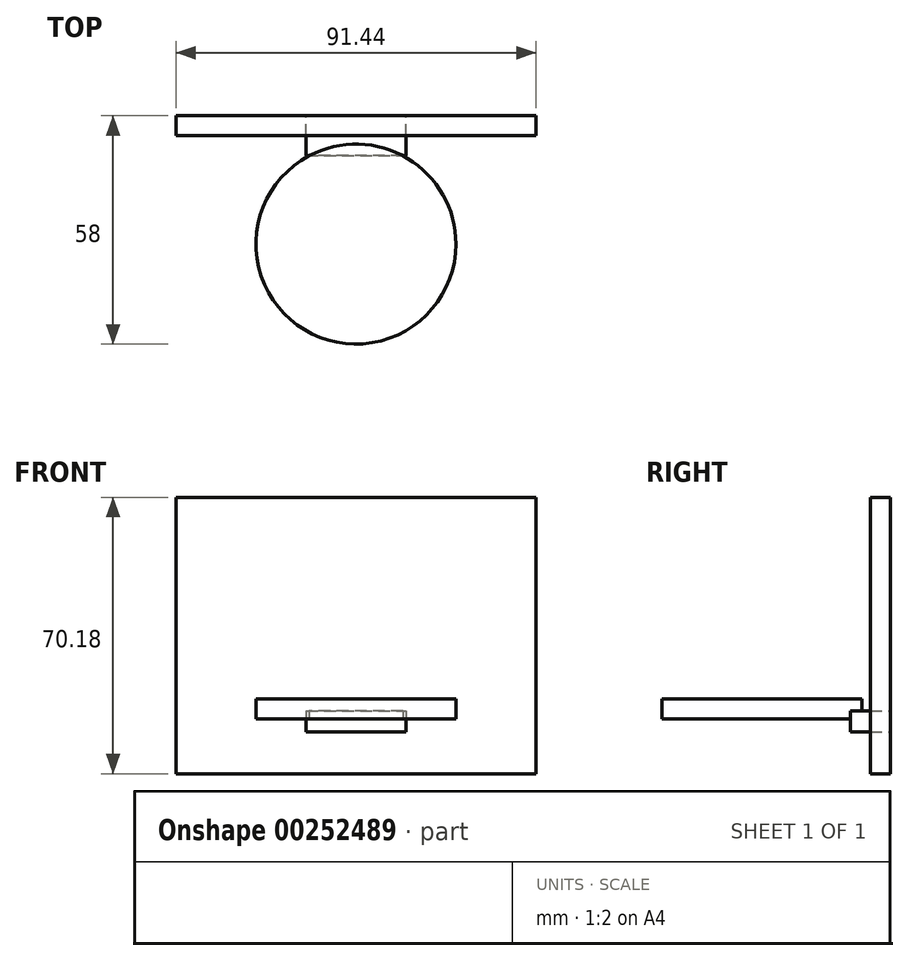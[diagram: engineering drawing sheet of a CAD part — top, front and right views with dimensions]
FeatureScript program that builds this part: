
annotation { "Feature Type Name" : "Feature", "Feature Type Description" : "" }
export const myFeature = defineFeature(function(context is Context, id is Id, definition is map)
    precondition{}
    {
        {
            var Q0;
            Q0=qCreatedBy(makeId("Front.planeOp"),FACE);
            var sketch = newSketch(context, id + "F0", { "sketchPlane" : qUnion([Q0])});
            skLineSegment(sketch, "E0.bottom", {"start": v(-45.72, 56.26) * mm, "end": v(45.72, 56.26) * mm});
            skLineSegment(sketch, "E0.top", {"start": v(-45.72, -13.92) * mm, "end": v(45.72, -13.92) * mm});
            skLineSegment(sketch, "E0.left", {"start": v(-45.72, 56.26) * mm, "end": v(-45.72, -13.92) * mm});
            skLineSegment(sketch, "E0.right", {"start": v(45.72, 56.26) * mm, "end": v(45.72, -13.92) * mm});
            skSolve(sketch);
        }
        {
            var Q0;
            Q0 = qSketchRegion(id + "F0", true);
            extrude(context, id + "F1", {"entities" : qUnion([Q0]), "depth" : 5.08 * mm});
        }
        {
            var Q0;
            Q0=qCreatedBy(makeId("Front.planeOp"),FACE);
            var sketch = newSketch(context, id + "F2", { "sketchPlane" : qUnion([Q0])});
            skLineSegment(sketch, "E1.bottom", {"start": v(-12.7, 2.04) * mm, "end": v(12.7, 2.04) * mm});
            skLineSegment(sketch, "E1.top", {"start": v(-12.7, -3.28) * mm, "end": v(12.7, -3.28) * mm});
            skLineSegment(sketch, "E1.left", {"start": v(-12.7, 2.04) * mm, "end": v(-12.7, -3.28) * mm});
            skLineSegment(sketch, "E1.right", {"start": v(12.7, 2.04) * mm, "end": v(12.7, -3.28) * mm});
            skSolve(sketch);
        }
        {
            var Q0;
            Q0 = qSketchRegion(id + "F2", true);
            extrude(context, id + "F3", {"entities" : qUnion([Q0]), "depth" : 10.16 * mm});
        }
        {
            var Q0;
            Q0=qCreatedBy(makeId("Top.planeOp"),FACE);
            var sketch = newSketch(context, id + "F4", { "sketchPlane" : qUnion([Q0])});
            skCircle(sketch, "E2", {"center": v(0, -32.6) * mm, "radius": 25.4 * mm});
            skSolve(sketch);
        }
        {
            var Q0;
            Q0 = qSketchRegion(id + "F4", true);
            extrude(context, id + "F5", {"entities" : qUnion([Q0]), "operationType" : NewBodyOperationType.ADD, "depth" : 5.08 * mm});
        }
        {
            var Q0;
            Q0=qCreatedBy(makeId("Top.planeOp"),FACE);
            var sketch = newSketch(context, id + "F6", { "sketchPlane" : qUnion([Q0])});
            skLineSegment(sketch, "E3", {"start": v(0, -7.2) * mm, "end": v(0, -57.95) * mm});
            skLineSegment(sketch, "E4", {"start": v(0, -57.95) * mm, "end": v(0, -32.58) * mm});
            skCircle(sketch, "E5", {"center": v(0, -32.58) * mm, "radius": 21.87 * mm});
            skSolve(sketch);
        }
        {
            var Q0;
            Q0 = qSketchRegion(id + "F6", true);
            extrude(context, id + "F7", {"entities" : qUnion([Q0]), "operationType" : NewBodyOperationType.REMOVE, "oppositeDirection" : true, "depth" : 5.08 * mm});
        }
    });
